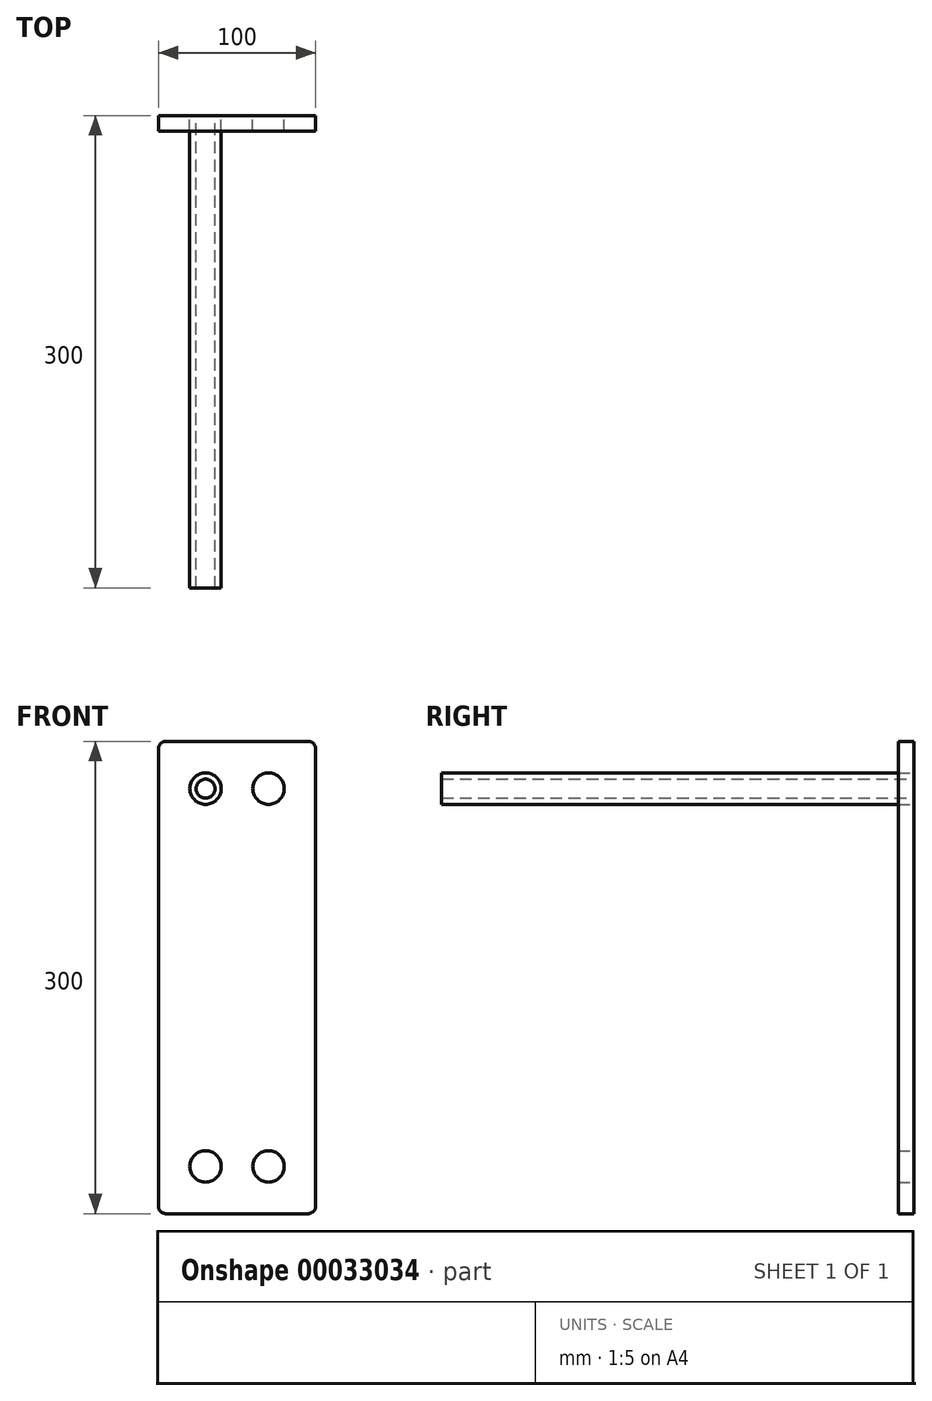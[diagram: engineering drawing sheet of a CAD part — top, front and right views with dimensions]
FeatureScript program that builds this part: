
annotation { "Feature Type Name" : "Feature", "Feature Type Description" : "" }
export const myFeature = defineFeature(function(context is Context, id is Id, definition is map)
    precondition{}
    {
        {
            var Q0;
            Q0=qCreatedBy(makeId("Front.planeOp"),FACE);
            var sketch = newSketch(context, id + "F0", { "sketchPlane" : qUnion([Q0])});
            skLineSegment(sketch, "E0.bottom", {"start": v(-58, 156.52) * mm, "end": v(32, 156.52) * mm});
            skLineSegment(sketch, "E0.top", {"start": v(-58, -143.48) * mm, "end": v(32, -143.48) * mm});
            skLineSegment(sketch, "E0.left", {"start": v(-63, 151.52) * mm, "end": v(-63, -138.48) * mm});
            skLineSegment(sketch, "E0.right", {"start": v(37, 151.52) * mm, "end": v(37, -138.48) * mm});
            skPoint(sketch, "E1.visualSharp", {"position": v(-63, 156.52) * mm});
            skArc(sketch, "E1.filletArc", {"start": v(-58, 156.52) * mm, "mid": v(-61.53, 155.05) * mm, "end": v(-63, 151.52) * mm});
            skPoint(sketch, "E2.visualSharp", {"position": v(37, 156.52) * mm});
            skArc(sketch, "E2.filletArc", {"start": v(37, 151.52) * mm, "mid": v(35.54, 155.05) * mm, "end": v(32, 156.52) * mm});
            skPoint(sketch, "E3.visualSharp", {"position": v(-63, -143.48) * mm});
            skArc(sketch, "E3.filletArc", {"start": v(-63, -138.48) * mm, "mid": v(-61.53, -142.02) * mm, "end": v(-58, -143.48) * mm});
            skPoint(sketch, "E4.visualSharp", {"position": v(37, -143.48) * mm});
            skArc(sketch, "E4.filletArc", {"start": v(32, -143.48) * mm, "mid": v(35.54, -142.02) * mm, "end": v(37, -138.48) * mm});
            skPoint(sketch, "E5", {"position": v(-13, 156.52) * mm});
            skCircle(sketch, "E6", {"center": v(-33, -113.48) * mm, "radius": 10 * mm});
            skCircle(sketch, "E7", {"center": v(7, -113.48) * mm, "radius": 10 * mm});
            skCircle(sketch, "E8", {"center": v(-33, -113.48) * mm, "radius": 6 * mm});
            skCircle(sketch, "E9", {"center": v(7, -113.48) * mm, "radius": 6 * mm});
            skCircle(sketch, "E10", {"center": v(-33, 126.52) * mm, "radius": 6 * mm});
            skCircle(sketch, "E11", {"center": v(7, 126.52) * mm, "radius": 6 * mm});
            skCircle(sketch, "E12", {"center": v(7, 126.52) * mm, "radius": 10 * mm});
            skCircle(sketch, "E13", {"center": v(-33, 126.52) * mm, "radius": 10 * mm});
            skSolve(sketch);
        }
        {
            var Q0;
            Q0=makeQuery(id+"F0.imprint","IMPRINT",FACE,{"disambiguationData":[TD([[makeQuery(id+"F0.imprint","IMPRINT",EDGE,{"derivedFrom":sQuery(id+"F0.wireOp",EDGE,"E0.bottom")}),-1.0]])]});
            extrude(context, id + "F1", {"entities" : qUnion([Q0]), "depth" : 10 * mm});
        }
        {
            var Q0;
            Q0=makeQuery(id+"F0.imprint","IMPRINT",FACE,{"disambiguationData":[TD([[makeQuery(id+"F0.imprint","IMPRINT",EDGE,{"derivedFrom":sQuery(id+"F0.wireOp",EDGE,"E10")}),-1.0]])]});
            extrude(context, id + "F2", {"entities" : qUnion([Q0]), "depth" : 300 * mm});
        }
    });
